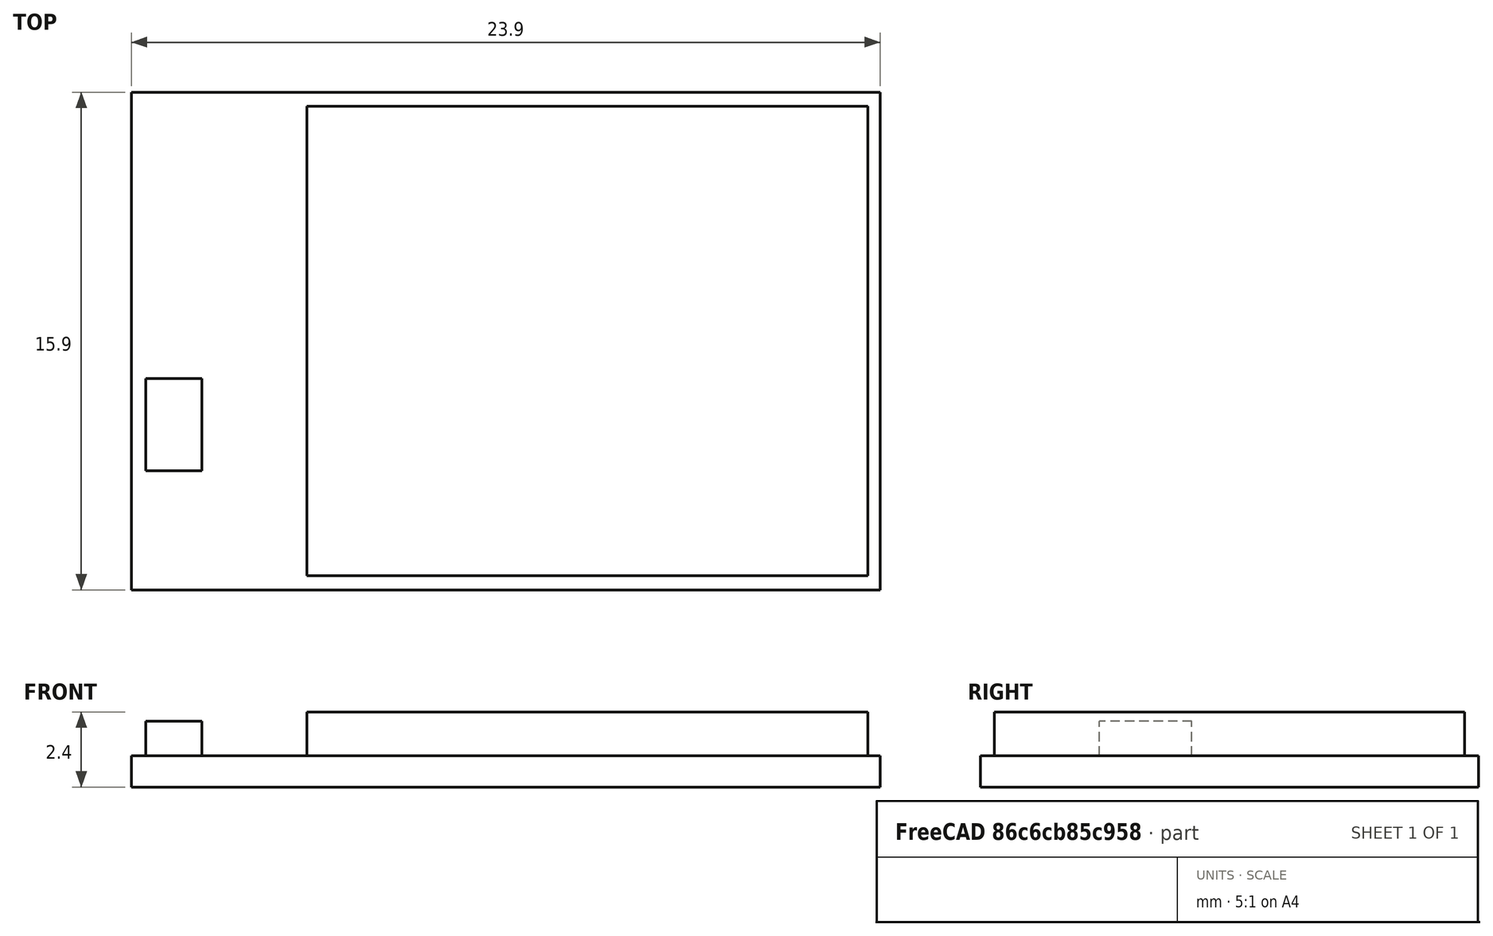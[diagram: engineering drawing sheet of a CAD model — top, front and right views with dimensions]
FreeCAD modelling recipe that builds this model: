
FCSTD DOCUMENT  (FreeCAD 0.17R)
Label: wt32i
License: All rights reserved
LicenseURL: http://en.wikipedia.org/wiki/All_rights_reserved
objects: Sketcher::SketchObject×3, PartDesign::Pad×3, PartDesign::Body×1, Mesh::Feature×1
note: 10 computed .brp shape members not serialized (recipe doc carries the construction recipe); baked Part::Feature solids carry a one-line shape summary decoded from their .brp

FEATURE [Sketcher::SketchObject] Sketch
  MapMode = 5
  Support = -> [XY_Plane]
  sketch-geometry (4):
    g0: LineSegment StartX=-11.95 StartY=7.95 StartZ=0 EndX=11.95 EndY=7.95 EndZ=0
    g1: LineSegment StartX=11.95 StartY=7.95 StartZ=0 EndX=11.95 EndY=-7.95 EndZ=0
    g2: LineSegment StartX=11.95 StartY=-7.95 StartZ=0 EndX=-11.95 EndY=-7.95 EndZ=0
    g3: LineSegment StartX=-11.95 StartY=-7.95 StartZ=0 EndX=-11.95 EndY=7.95 EndZ=0
  constraints (11):
    c: Coincident(g0,g1)
    c: Coincident(g1,g2)
    c: Coincident(g2,g3)
    c: Coincident(g3,g0)
    c: Horizontal(g0)
    c: Horizontal(g2)
    c: Vertical(g1)
    c: Vertical(g3)
    c: DistanceX(g0,g0) = 23.9
    c: DistanceY(g3,g3) = 15.9
    c: Symmetric(g0,g1,g-1)
FEATURE [PartDesign::Pad] Pad
  Length = 1
  Length2 = 100
  Profile = -> Sketch
  Refine = true
  Type = 0
FEATURE [Sketcher::SketchObject] Sketch001
  ExternalGeometry = -> [Pad]
  MapMode = 5
  Placement = pos=(0,0,1) rot=(0,0,1;0rad)
  Support = -> [Pad]
  sketch-geometry (4):
    g0: LineSegment StartX=-6.35 StartY=7.5 StartZ=0 EndX=11.55 EndY=7.5 EndZ=0
    g1: LineSegment StartX=11.55 StartY=7.5 StartZ=0 EndX=11.55 EndY=-7.5 EndZ=0
    g2: LineSegment StartX=11.55 StartY=-7.5 StartZ=0 EndX=-6.35 EndY=-7.5 EndZ=0
    g3: LineSegment StartX=-6.35 StartY=-7.5 StartZ=0 EndX=-6.35 EndY=7.5 EndZ=0
  constraints (12):
    c: Coincident(g0,g1)
    c: Coincident(g1,g2)
    c: Coincident(g2,g3)
    c: Coincident(g3,g0)
    c: Horizontal(g0)
    c: Horizontal(g2)
    c: Vertical(g1)
    c: Vertical(g3)
    c: DistanceX(g0,g0) = 17.9
    c: DistanceY(g3,g3) = 15
    c: DistanceX(g-4,g2) = 5.6
    c: DistanceY(g-4,g2) = 0.45
FEATURE [PartDesign::Pad] Pad001
  BaseFeature = -> Pad
  Length = 1.4
  Length2 = 100
  Profile = -> Sketch001
  Refine = true
  Type = 0
FEATURE [Sketcher::SketchObject] Sketch002
  ExternalGeometry = -> [Pad001]
  MapMode = 5
  Placement = pos=(0,0,1) rot=(0,0,1;0rad)
  Support = -> [Pad001]
  sketch-geometry (4):
    g0: LineSegment StartX=-11.5 StartY=-1.2 StartZ=0 EndX=-9.7 EndY=-1.2 EndZ=0
    g1: LineSegment StartX=-9.7 StartY=-1.2 StartZ=0 EndX=-9.7 EndY=-4.15 EndZ=0
    g2: LineSegment StartX=-9.7 StartY=-4.15 StartZ=0 EndX=-11.5 EndY=-4.15 EndZ=0
    g3: LineSegment StartX=-11.5 StartY=-4.15 StartZ=0 EndX=-11.5 EndY=-1.2 EndZ=0
  constraints (12):
    c: Coincident(g0,g1)
    c: Coincident(g1,g2)
    c: Coincident(g2,g3)
    c: Coincident(g3,g0)
    c: Horizontal(g0)
    c: Horizontal(g2)
    c: Vertical(g1)
    c: Vertical(g3)
    c: DistanceX(g0,g-3) = 3.35
    c: DistanceY(g-4,g2) = 3.8
    c: DistanceY(g0,g-5) = 9.15
    c: DistanceX(g-5,g0) = 0.45
FEATURE [PartDesign::Pad] Pad002
  BaseFeature = -> Pad001
  Length = 1.1
  Length2 = 100
  Profile = -> Sketch002
  Refine = true
  Type = 0
FEATURE [PartDesign::Body] Body
  Group = -> [Sketch,Pad,Sketch001,Pad001,Sketch002,Pad002]
  Origin = -> Origin
  Tip = -> Pad002
FEATURE [Mesh::Feature] Mesh  label="Pad002 (Meshed)"
